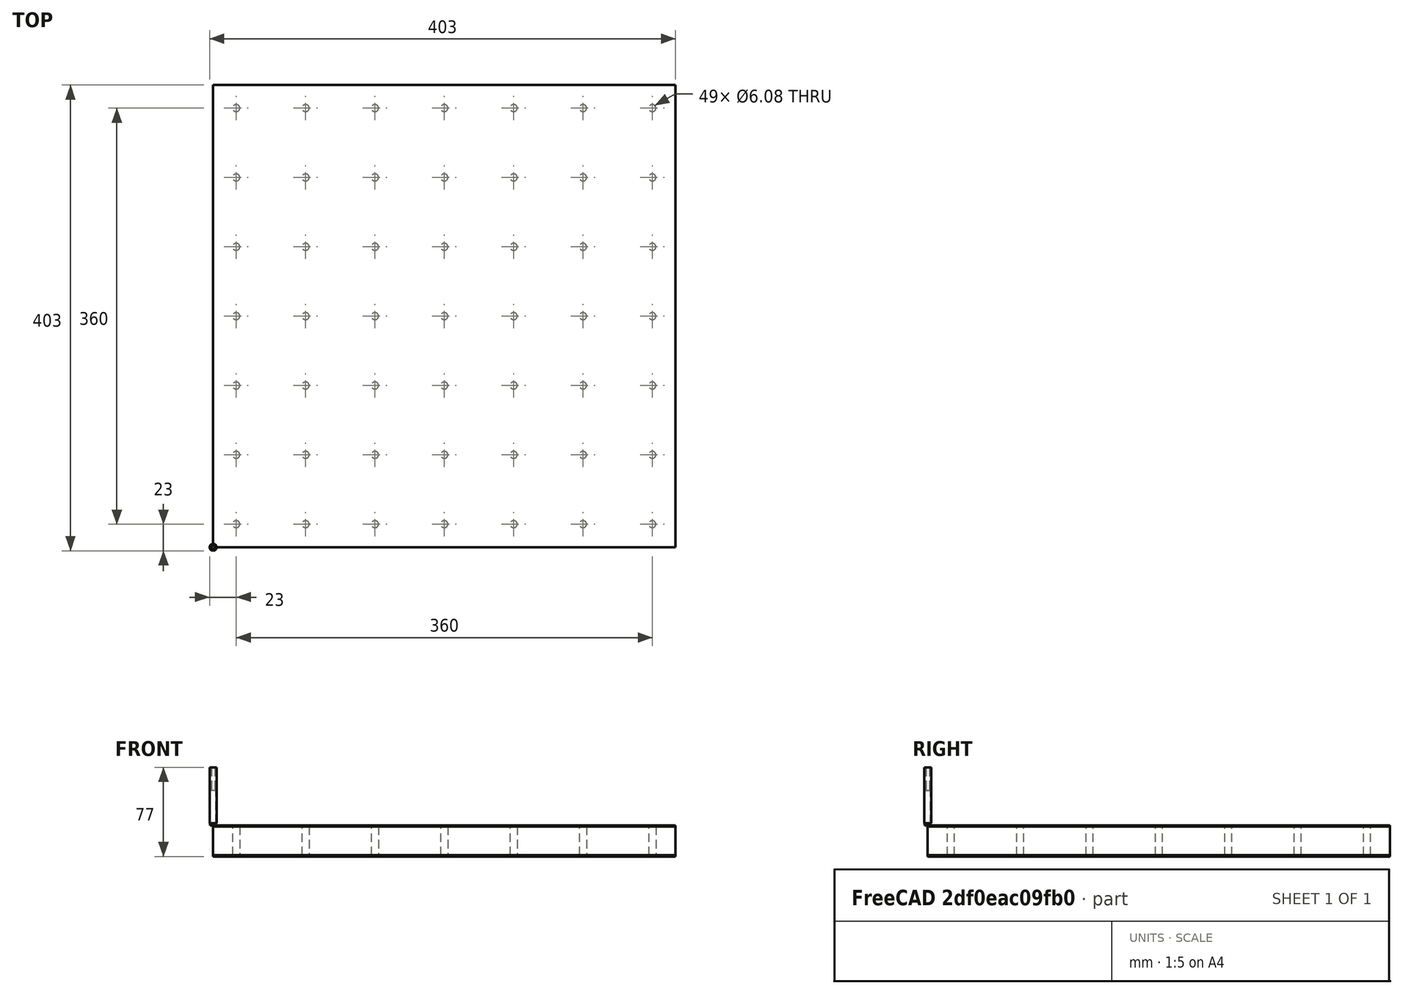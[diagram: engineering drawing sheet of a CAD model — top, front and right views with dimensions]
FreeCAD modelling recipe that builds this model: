
FCSTD DOCUMENT  (FreeCAD 0.19R23463 (Git))
Label: trous6mmDansPlan
License: All rights reserved
LicenseURL: http://en.wikipedia.org/wiki/All_rights_reserved
objects: Part::FeaturePython×4, Path::FeaturePython×4, Sketcher::SketchObject×2, PartDesign::LinearPattern×2, PartDesign::Pad×1, PartDesign::Pocket×1, PartDesign::MultiTransform×1, PartDesign::Body×1, App::FeaturePython×1, App::DocumentObjectGroup×1, Path::FeatureCompoundPython×1, Mesh::FeaturePython×1
note: 14 computed .brp shape members not serialized (recipe doc carries the construction recipe); baked Part::Feature solids carry a one-line shape summary decoded from their .brp

FEATURE [Sketcher::SketchObject] Sketch
  MapMode = 5
  Support = -> [XY_Plane]
  sketch-geometry (4):
    g0: LineSegment StartX=0 StartY=0 StartZ=0 EndX=400 EndY=0 EndZ=0
    g1: LineSegment StartX=400 StartY=0 StartZ=0 EndX=400 EndY=400 EndZ=0
    g2: LineSegment StartX=400 StartY=400 StartZ=0 EndX=0 EndY=400 EndZ=0
    g3: LineSegment StartX=0 StartY=400 StartZ=0 EndX=0 EndY=0 EndZ=0
  constraints (11):
    c: Coincident(g0,g1)
    c: Coincident(g1,g2)
    c: Coincident(g2,g3)
    c: Coincident(g3,g0)
    c: Horizontal(g0)
    c: Horizontal(g2)
    c: Vertical(g1)
    c: Vertical(g3)
    c: Coincident(g0,g-1)
    c: DistanceX(g-1,g0) = 400
    c: DistanceY(g-1,g1) = 400
FEATURE [PartDesign::Pad] Pad
  Direction = (1,1,1)
  Length = 25
  Length2 = 100
  Profile = -> Sketch
  Type = 0
FEATURE [Sketcher::SketchObject] Sketch001
  MapMode = 5
  Placement = pos=(0,0,25) rot=(0,0,1;0rad)
  Support = -> [Pad]
  sketch-geometry (1):
    g0: Circle CenterX=20 CenterY=20 CenterZ=0 NormalX=0 NormalY=0 NormalZ=1 AngleXU=0 Radius=3.04004
FEATURE [PartDesign::Pocket] Pocket
  BaseFeature = -> Pad
  Length = 5
  Length2 = 100
  Profile = -> Sketch001
  Type = 1
FEATURE [PartDesign::LinearPattern] LinearPattern
  Direction = -> Sketch001 [H_Axis]
  Length = 360
  Occurrences = 7
FEATURE [PartDesign::LinearPattern] LinearPattern001
  Direction = -> Sketch001 [V_Axis]
  Length = 360
  Occurrences = 7
FEATURE [PartDesign::MultiTransform] MultiTransform
  BaseFeature = -> Pocket
  Originals = -> [Pocket]
  Transformations = -> [LinearPattern,LinearPattern001]
FEATURE [PartDesign::Body] Body
  Group = -> [Sketch,Pad,Sketch001,Pocket,MultiTransform,LinearPattern,LinearPattern001]
  Origin = -> Origin
  Tip = -> MultiTransform
FEATURE [App::FeaturePython] SetupSheet  # Path/CAM operation (typed FeaturePython)
  ClearanceHeightExpression = OpStockZMax+SetupSheet.ClearanceHeightOffset
  ClearanceHeightOffset = 5
  CoolantMode = 0
  CoolantModes = None | Flood | Mist
  FinalDepthExpression = OpFinalDepth
  HorizRapid = 0
  SafeHeightExpression = OpStockZMax+SetupSheet.SafeHeightOffset
  SafeHeightOffset = 3
  StartDepthExpression = OpStartDepth
  StepDownExpression = OpToolDiameter
  VertRapid = 0
FEATURE [Part::FeaturePython] Clone  label="Model-Body"  # Draft clone (typed FeaturePython)
  AttacherType = Attacher::AttachEngine3D
  Fuse = false
  Objects = -> [Body]
  PathResource = Model
  Placement = pos=(0,0,-26) rot=(0,0,1;0rad)
  Scale = (1,1,1)
FEATURE [App::DocumentObjectGroup] Model
  Group = -> [Clone]
FEATURE [Part::FeaturePython] ToolBit  label="Endmill"  # Path/CAM toolbit (typed FeaturePython)
  BitShape = /Volumes/SSD/Applications/FreeCAD-0_19.app/Contents/Resources/Mod/Path/Tools/Shape/endmill.fcstd
  CuttingEdgeHeight = 30
  Diameter = 5
  Length = 50
  ShankDiameter = 3
  ShapeName = endmill
FEATURE [Path::FeaturePython] TC__Default_Tool  label="TC: Default Tool"  # Path/CAM operation (typed FeaturePython)
  HorizFeed = 0
  HorizRapid = 0
  SpindleDir = 0
  SpindleSpeed = 0
  Tool = -> ToolBit
  ToolNumber = 1
  VertFeed = 0
  VertRapid = 0
  expr: HorizRapid = SetupSheet.HorizRapid
  expr: VertRapid = SetupSheet.VertRapid
FEATURE [Part::FeaturePython] Stock  # WARN: FeaturePython — macro-defined, semantics opaque (R4)
  Base = -> Model
  ExtXneg = 0
  ExtXpos = 0
  ExtYneg = 0
  ExtYpos = 0
  ExtZneg = 1
  ExtZpos = 1
  Placement = pos=(0,0,-26) rot=(0,0,1;0rad)
  StockType = FromBase
FEATURE [Part::FeaturePython] ToolBit001  label="6mm_drill"  # Path/CAM toolbit (typed FeaturePython)
  BitShape = /Volumes/SSD/Applications/FreeCAD-0_19.app/Contents/Resources/Mod/Path/Tools/Shape/drill.fcstd
  Diameter = 6
  File = /Volumes/SSD/Applications/FreeCAD-0_19.app/Contents/Resources/Mod/Path/Tools/Bit/6mm_drill.fctb
  Length = 50
  ShapeName = drill
  TipAngle = 119
FEATURE [Path::FeaturePython] TC__6mm_drill  label="TC: 6mm_drill"  # Path/CAM operation (typed FeaturePython)
  HorizFeed = 5
  HorizRapid = 10
  SpindleDir = 0
  SpindleSpeed = 0
  Tool = -> ToolBit001
  ToolNumber = 9
  VertFeed = 5
  VertRapid = 10
  expr: HorizRapid = 10
  expr: VertRapid = 10
FEATURE [Path::FeaturePython] Drilling  # Path/CAM operation (typed FeaturePython)
  Active = true
  AddTipLength = false
  AttemptInverseAngle = false
  Base = -> [Clone]
  ClearanceHeight = 5
  CoolantMode = None
  CycleTime = 00:02:22
  DwellEnabled = false
  DwellTime = 1
  EnableRotation = 0
  ExtraOffset = 0
  FinalDepth = -26
  InverseAngle = false
  OpFinalDepth = -26
  OpStartDepth = 0
  OpStockZMax = 0
  OpStockZMin = -27
  OpToolDiameter = 6
  PeckDepth = 4.5
  PeckEnabled = false
  RetractHeight = 1
  ReturnLevel = 0
  ReverseDirection = false
  SafeHeight = 3
  StartDepth = 0
  ToolController = -> TC__6mm_drill
  expr: PeckDepth = OpToolDiameter * 0.75
  expr: RetractHeight = OpStartDepth + 1mm
  expr: ClearanceHeight = OpStockZMax + SetupSheet.ClearanceHeightOffset
  expr: SafeHeight = OpStockZMax + SetupSheet.SafeHeightOffset
  expr: StartDepth = OpStartDepth
FEATURE [Path::FeatureCompoundPython] Operations  # Path/CAM operation (typed FeaturePython)
  Group = -> [Drilling]
  UsePlacements = false
FEATURE [Path::FeaturePython] Job  # Path/CAM operation (typed FeaturePython)
  CycleTime = 00:02:22
  Fixtures = G54
  GeometryTolerance = 0.01
  LastPostProcessDate = 2021-02-04 16:19:44.441135
  LastPostProcessOutput = /Volumes/SSD/Dev/CNC/MiscCNC/trous6mmDansPlan.gcode
  Model = -> Model
  Operations = -> Operations
  OrderOutputBy = 0
  PostProcessor = 12
  PostProcessorOutputFile = /Volumes/SSD/Dev/CNC/MiscCNC/trous6mmDansPlan.gcode
  SetupSheet = -> SetupSheet
  SplitOutput = false
  Stock = -> Stock
  ToolController = -> [TC__Default_Tool,TC__6mm_drill]
FEATURE [Mesh::FeaturePython] CutMaterial  # WARN: FeaturePython — macro-defined, semantics opaque (R4)
